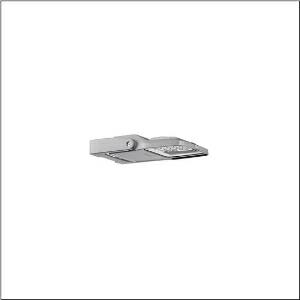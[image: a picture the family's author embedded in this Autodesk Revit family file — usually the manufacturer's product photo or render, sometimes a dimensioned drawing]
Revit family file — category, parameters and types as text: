
# Revit family: floodlight_fl_21_iq_micro___pl43_5xa7762a2a2a_df73
name_source: partatom
category: Lighting Fixtures
units: mm (PartAtom-declared; Revit-internal decimal feet)

## family parameters
Cut with Voids When Loaded = No
Host = Face
Light Source = No
Part Type = Normal
Room Calculation Point = No
Round Connector Dimension = Use Diameter
Shared = No

## types (1)
- --- (1 x LED, 3040 lm, 23.1 W, 3000K)
    Apparent Load = 23 VA
    CIE Flux Codes = 29 80 99 100 100
    Color Rendering = 70
    Color Temperature = 3000K
    Default Elevation = 1800 mm
    Description = Floodlight FL 21 iQ micro, floodlight, primary light control with lens, of PMMA, primary optical cover: protective disc, of toughened safety glass, transparent, light distribution: PL43, light emission: direct distribution, installation type: surface-mounted, LED, High Power LED, rated luminous flux: 3.040lm, luminous efficacy: 132lm/W, light colour: 730, colour temperature: 3000K, control gear: iQ Street-Remote/DALI, control: Auto-Match, Temp-Guard, Night-Set, Smart-Wire, Desk-Remote (wireless, voltage-free reading and setting of iQ features in the workshop via application-optimized NFC function/RFID function), optimised constant luminous flux control (CLO 2.0), Street-Remote, with terminal, 6-pole, mains connection: 220..240V, AC, 50/60Hz, start of lifetime: 23W, end of service life: 24W, reduction: 11W, luminaire housing, of diecast aluminium, powder-coated, Siteco® metallic grey (DB 702S), corrosivity category C5 mid according to DIN EN ISO 12944, suitable for swimming pools, chlorine-resistant, sealing non-destructively replaceable, design bracket, of diecast aluminium, powder-coated, Siteco® metallic grey (DB 702S), protection rating (complete): IP66, insulation class (complete): insulation class II (safety insulation), certification: CE, ENEC, VDE, protection symbol: D, impact resistance: IK07, permissible operating ambient temperature: -40..+40°C, permissible operating ambient temperature for outdoor applications: -40..+50°C, standard: DIN EN 12944, LABS conformity tested according to VDMA 24364:2018-05, packaging unit: 1 piece

Light Distribution: PL43
    Height = 65 mm
    Lamp = 1 x LED
    Lamp Light Flux = 3040 lm
    Lamp Power = 23.1 W
    Lamp count = 1
    Length = 312 mm
    Luminous efficacy = 132 lm/W
    Manufacturer = Siteco
    ModVariant = No
    Model = 5XA7762A2A2A
    Mounting Place = Wall
    Mounting Type = Surface mounted
    Number of Poles = 1
    OnlyDefault = Yes
    Power Factor = 1
    Product Name = Floodlight FL 21 iQ micro | PL43
    Product group = floodlight | wall mounted
    ProductGroupID = 2001
    Protection Class = Protection class II
    Protection Degree = IP 66
    RLX_Detail_Level = 1
    RLX_Emergency_Light_Flux = 0 lm
    RLX_Emergency_Type = 0
    RLX_Emergency_Type_DB = No
    RlxData = <blob elided: 97481 chars, md5=aae57306>
    Socket = socket
    Standby Power = 0 W
    System Light Flux = 3040 lm
    System Power = 23 W
    Type Comments = factory setting: luminous flux: 100 % | dim-lin: 254 | 455 mA
    Type Image = l_1006878.jpg
    URL = http://relux.com
    VarID = @adj_198085
    Voltage = 0 V
    Weight = 0.00 kg
    Width = 230 mm

## geometry (parser evidence)
native form markers: Blend x4, Sweep x11
no freeform markers — native parametric forms only
